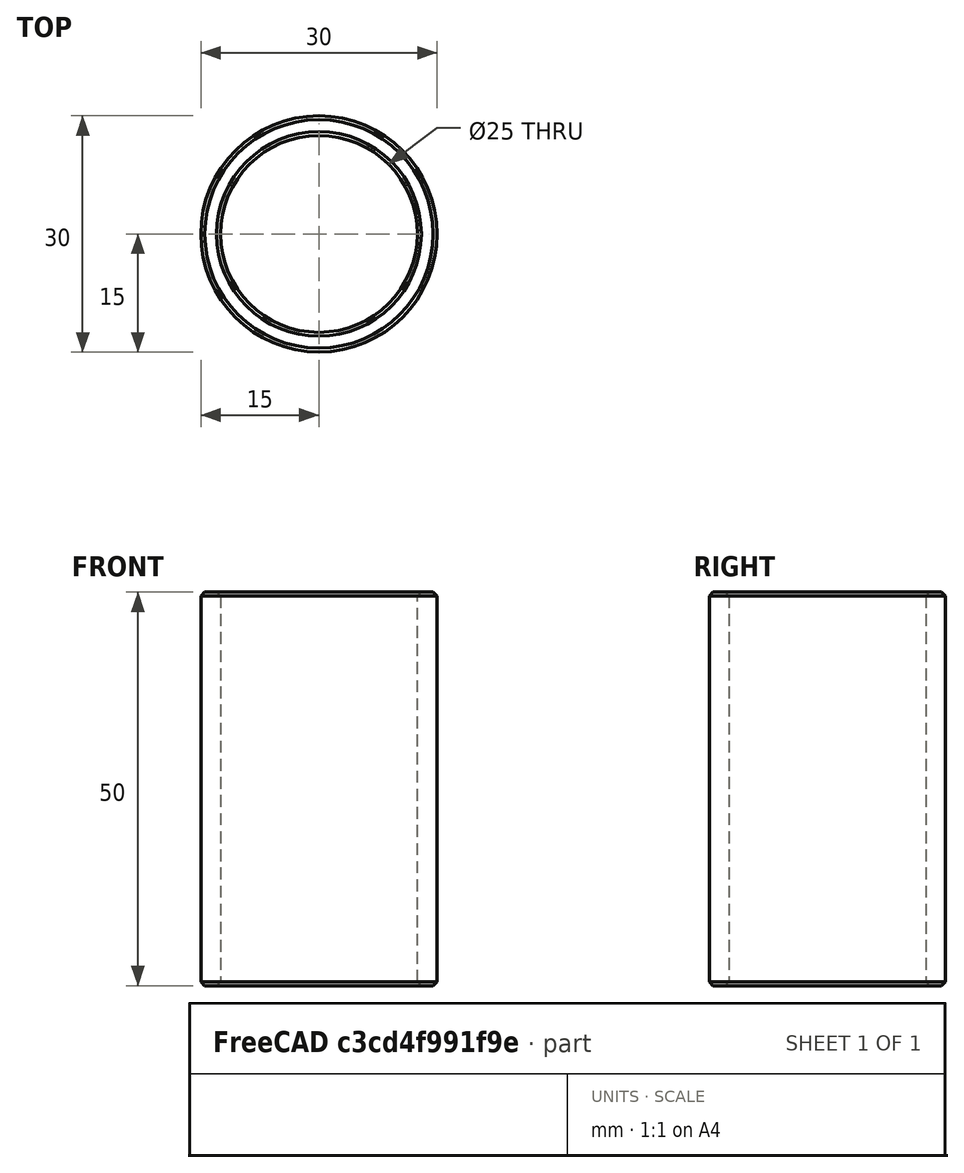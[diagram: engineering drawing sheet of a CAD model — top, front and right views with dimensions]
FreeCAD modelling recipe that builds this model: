
FCSTD DOCUMENT  (FreeCAD 0.20R29177 +426 (Git))
Label: hovairGuidageBague
License: All rights reserved
LicenseURL: http://en.wikipedia.org/wiki/All_rights_reserved
objects: TechDraw::DrawViewDimension×4, Sketcher::SketchObject×1, PartDesign::Pad×1, PartDesign::Chamfer×1, PartDesign::Body×1, TechDraw::DrawSVGTemplate×1, TechDraw::DrawProjGroupItem×1, TechDraw::DrawProjGroup×1, TechDraw::DrawViewSection×1, TechDraw::DrawViewAnnotation×1, TechDraw::DrawPage×1
note: 6 computed .brp shape members not serialized (recipe doc carries the construction recipe); baked Part::Feature solids carry a one-line shape summary decoded from their .brp

FEATURE [Sketcher::SketchObject] Sketch
  FullyConstrained = true
  MapMode = 5
  Support = -> [XY_Plane]
  sketch-geometry (2):
    g0: Circle CenterX=0 CenterY=0 CenterZ=0 NormalX=0 NormalY=0 NormalZ=1 AngleXU=0 Radius=15
    g1: Circle CenterX=0 CenterY=0 CenterZ=0 NormalX=0 NormalY=0 NormalZ=1 AngleXU=0 Radius=12.5
  constraints (4):
    c: Coincident(g1,g0)
    c: Coincident(g0,g-1)
    c: Diameter(g1) = 25
    c: Diameter(g0) = 30
FEATURE [PartDesign::Pad] Pad
  Direction = (0,0,1)
  Length = 50
  Length2 = 10
  Profile = -> Sketch
  ReferenceAxis = -> Sketch [N_Axis]
  Type = 0
FEATURE [PartDesign::Chamfer] Chamfer
  Angle = 45
  Base = -> Pad [Edge3,Edge6,Edge2,Edge5]
  BaseFeature = -> Pad
  ChamferType = 0
  FlipDirection = false
  Size = 0.5
  Size2 = 1
  SupportTransform = false
  UseAllEdges = false
FEATURE [PartDesign::Body] Body  label="hovairGuidageBague"
  Group = -> [Sketch,Pad,Chamfer]
  Origin = -> Origin
  Tip = -> Chamfer
FEATURE [TechDraw::DrawSVGTemplate] Template
  EditableTexts = Designed_by_Name=Designed by Name; Drawing_number=Drawing number; FC-Date=Date; FC-SC=Scale; FC-SH=Sheet; FC-Title=Title; Subtitle=Subtitle; Weight=Weight
  Height = 210
  Orientation = 1
  Width = 297
FEATURE [TechDraw::DrawProjGroupItem] ProjItem  label="Front"
  CoarseView = false
  Direction = (0,0,1)
  Focus = 100
  HardHidden = false
  IsoCount = 0
  IsoHidden = false
  IsoVisible = true
  LockPosition = true
  Perspective = false
  Rotation = 0
  RotationVector = (1,0,0)
  Scale = 2
  ScaleType = 2
  SeamHidden = false
  SeamVisible = true
  SmoothHidden = false
  SmoothVisible = true
  Source = -> [Chamfer]
  Type = 0
  X = 0
  XDirection = (1,0,0)
  Y = 0
FEATURE [TechDraw::DrawProjGroup] ProjGroup
  Anchor = -> ProjItem
  AutoDistribute = true
  LockPosition = false
  ProjectionType = 0
  Rotation = 0
  Scale = 2
  ScaleType = 0
  Source = -> [Chamfer]
  Views = -> [ProjItem]
  X = 231.503
  Y = 121.721
  spacingX = 15
  spacingY = 15
FEATURE [TechDraw::DrawViewSection] SectionView  label="Section  - "
  BaseView = -> ProjItem
  CoarseView = false
  CutSurfaceDisplay = 2
  Direction = (1,0,0)
  FileGeomPattern = C:/Program Files/FreeCAD 0.21/data/Mod/TechDraw/PAT/FCPAT.pat
  FileHatchPattern = C:/Program Files/FreeCAD 0.21/data/Mod/TechDraw/Patterns/simple.svg
  Focus = 100
  FuseBeforeCut = false
  HardHidden = false
  HatchScale = 1
  IsoCount = 0
  IsoHidden = false
  IsoVisible = true
  LockPosition = false
  NameGeomPattern = Diamant
  Perspective = false
  Rotation = 90
  Scale = 2
  ScaleType = 2
  SeamHidden = false
  SeamVisible = true
  SectionDirection = -1
  SectionNormal = (1,0,0)
  SectionOrigin = (0,0,25)
  SectionSymbol = A
  SmoothHidden = false
  SmoothVisible = true
  Source = -> [Chamfer]
  X = 117.916
  XDirection = (0,1,0)
  Y = 121.721
FEATURE [TechDraw::DrawViewDimension] Dimension
  AngleOverride = false
  Arbitrary = false
  ArbitraryTolerances = false
  EqualTolerance = true
  ExtensionAngle = 0
  FormatSpec = %.2w
  FormatSpecOverTolerance = %+.2w
  FormatSpecUnderTolerance = %+.2w
  Inverted = false
  LineAngle = 0
  LockPosition = false
  MeasureType = 1
  OverTolerance = 0
  References2D = -> [SectionView]
  Rotation = 0
  Scale = 2
  ScaleType = 0
  TheoreticalExact = false
  Type = 1
  UnderTolerance = 0
  X = -2.92302
  Y = 52.8534
FEATURE [TechDraw::DrawViewDimension] Dimension001
  AngleOverride = false
  Arbitrary = true
  ArbitraryTolerances = false
  EqualTolerance = true
  ExtensionAngle = 0
  FormatSpec = 4 x (0.5x45°)
  FormatSpecOverTolerance = %+.2w
  FormatSpecUnderTolerance = %+.2w
  Inverted = false
  LineAngle = 0
  LockPosition = false
  MeasureType = 1
  OverTolerance = 0
  References2D = -> [SectionView]
  Rotation = 0
  Scale = 2
  ScaleType = 0
  TheoreticalExact = false
  Type = 1
  UnderTolerance = 0
  X = -74.6753
  Y = -60.6495
FEATURE [TechDraw::DrawViewAnnotation] Annotation
  Font = osifont
  LineSpace = 100
  LockPosition = false
  MaxWidth = -1
  Rotation = 0
  Scale = 2
  ScaleType = 0
  Text = A - A
  TextSize = 5
  TextStyle = 0
  X = 114.871
  Y = 192.952
FEATURE [TechDraw::DrawViewDimension] Dimension002
  AngleOverride = false
  Arbitrary = true
  ArbitraryTolerances = false
  EqualTolerance = true
  ExtensionAngle = 0
  FormatSpec = Ø25 E8
  FormatSpecOverTolerance = %+.2w
  FormatSpecUnderTolerance = %+.2w
  Inverted = false
  LineAngle = 0
  LockPosition = false
  MeasureType = 1
  OverTolerance = 0
  References2D = -> [SectionView]
  Rotation = 0
  Scale = 2
  ScaleType = 0
  TheoreticalExact = false
  Type = 2
  UnderTolerance = 0
  X = -74.8981
  Y = 2.9427
FEATURE [TechDraw::DrawViewDimension] Dimension003
  AngleOverride = false
  Arbitrary = true
  ArbitraryTolerances = false
  EqualTolerance = false
  ExtensionAngle = 0
  FormatSpec = Ø30 
  FormatSpecOverTolerance = %+.2w
  FormatSpecUnderTolerance = %+.2w
  Inverted = false
  LineAngle = 0
  LockPosition = false
  MeasureType = 1
  OverTolerance = 0.05
  References2D = -> [SectionView]
  Rotation = 0
  Scale = 2
  ScaleType = 0
  TheoreticalExact = false
  Type = 2
  UnderTolerance = 0
  X = -97.476
  Y = 3.82811
FEATURE [TechDraw::DrawPage] Page
  KeepUpdated = true
  NextBalloonIndex = 1
  ProjectionType = 0
  Scale = 2
  Template = -> Template
  Views = -> [ProjGroup,SectionView,Dimension,Dimension001,Annotation,Dimension002,Dimension003]
